# Revit family: RN 81122 Optipress-Aquaplus-Schiebemuffe
name_source: partatom
category: Rohrformteile
units: mm (PartAtom-declared; Revit-internal decimal feet)

## family parameters
Arbeitsebenenbasiert = Nein
Beim Laden mit Abzugskörper schneiden = Nein
Bemaßung runder Anschluss = Durchmesser verwenden
Gemeinsam genutzt = Nein
Immer vertikal = Ja
Teiletyp = Verbindung

## types (3) — shared parameters
1.010.00.2 Blattnummer der Richtlinie = 29
1.010.00.3 Ausgabedatum (Monat) der Richtlinie = 201308
1.010.00.4 Herstellername = R. Nussbaum AG
1.010.00.5 Revisionsdatum der Datei = 20190521
1.010.00.6 Webadresse des Herstellers = http://www.nussbaum.ch
1.100.00.4 Produktbezeichnung = Versorgung
1.110.00.2 Index = 4
1.110.00.4 Produktbezeichnung = Optipress
1.960/3L.00.8 Link (URL) = https://www.nussbaum.ch
29.700.00.4 Produktname = Optipress-Aquaplus-Schiebemuffe, mit Einsteckende
29.700.00.5 Produktkennung = 2
29.700.00.6 Querschnittsform = 1
29.700.00.7 Nennweitensystem = DN
29.700.00.8 Nenndrucksystem = PN
29.710.02.4 Nenndruck = 16
29.710.02.5 max. zul. Überdruck [hPa] = 1600
29.710.02.7 max. zul. Dauer-Betriebsdruck [hPa] = 1600
29.710.02.9 max. zul. Dauer-Betriebstemperatur [°C] = 95
Connector Visibility = Nein
EnclosingSpace Visibility = Nein

## per-type parameters (varying)
| type | 1.800.00.3 TGA-Nummer | 1.810.00.3 Hersteller-Bestellnummer | 1.810.00.4 DATANORM-Nummer | 1.810.00.5 StLB-Nummer | 1.810.00.6 GTIN-Nummer | 29.710.02.10 Formstück-Gewicht [kg] | 29.710.02.3 Benennung | CONNECTOR0_DIAMETER_dX_0r | CONNECTOR0_dX_01 | CONNECTOR0_ref_dX | CONNECTOR1_DIAMETER_dX_0r | CONNECTOR1_dX_00 | CONNECTOR1_dX_01 | CONNECTOR1_ref_dX | R. Nussbaum AG 81122.24 de Visibility | R. Nussbaum AG 81122.25 de Visibility | R. Nussbaum AG 81122.26 de Visibility |
| 81122.24, Optipress-Aquaplus-Schiebemuffe, mit Einsteckende, DN=20, L=115 | 01900400000000000000000000000000000000000000000058000000000000000001 | 81122.24 | 81122.24 | 265.214 | 7612945682697 | 0.161 | Optipress-Aquaplus-Schiebemuffe, mit Einsteckende, DN=20, L=115 | 20 mm | 24 mm | 24 mm | 20 mm | 91 mm  [stored 0.298556 ft] | 115 mm | 91 mm  [stored 0.298556 ft] | Ja | Nein | Nein |
| 81122.25, Optipress-Aquaplus-Schiebemuffe, mit Einsteckende, DN=25, L=125 | 01900400000000000000000000000000000000000000000058000000000000000002 | 81122.25 | 81122.25 | 265.215 | 7612945682703 | 0.242 | Optipress-Aquaplus-Schiebemuffe, mit Einsteckende, DN=25, L=125 | 25 mm  [stored 0.082021 ft] | 24 mm | 24 mm | 25 mm  [stored 0.082021 ft] | 101 mm | 125 mm | 101 mm | Nein | Ja | Nein |
| 81122.26, Optipress-Aquaplus-Schiebemuffe, mit Einsteckende, DN=32, L=135 | 01900400000000000000000000000000000000000000000058000000000000000003 | 81122.26 | 81122.26 | 265.216 | 7612945682710 | 0.344 | Optipress-Aquaplus-Schiebemuffe, mit Einsteckende, DN=32, L=135 | 32 mm | 26 mm | 26 mm | 32 mm | 109 mm  [stored 0.357612 ft] | 135 mm | 109 mm  [stored 0.357612 ft] | Nein | Nein | Ja |

note: column(s) folded — value = type name in every type: 1.800.00.4 Kommentarfeld

note: [stored X ft] marks values corroborated as IEEE doubles in the binary element streams (Revit-internal decimal feet)

## geometry (parser evidence)
native form markers: Sweep x2
no freeform markers — native parametric forms only
